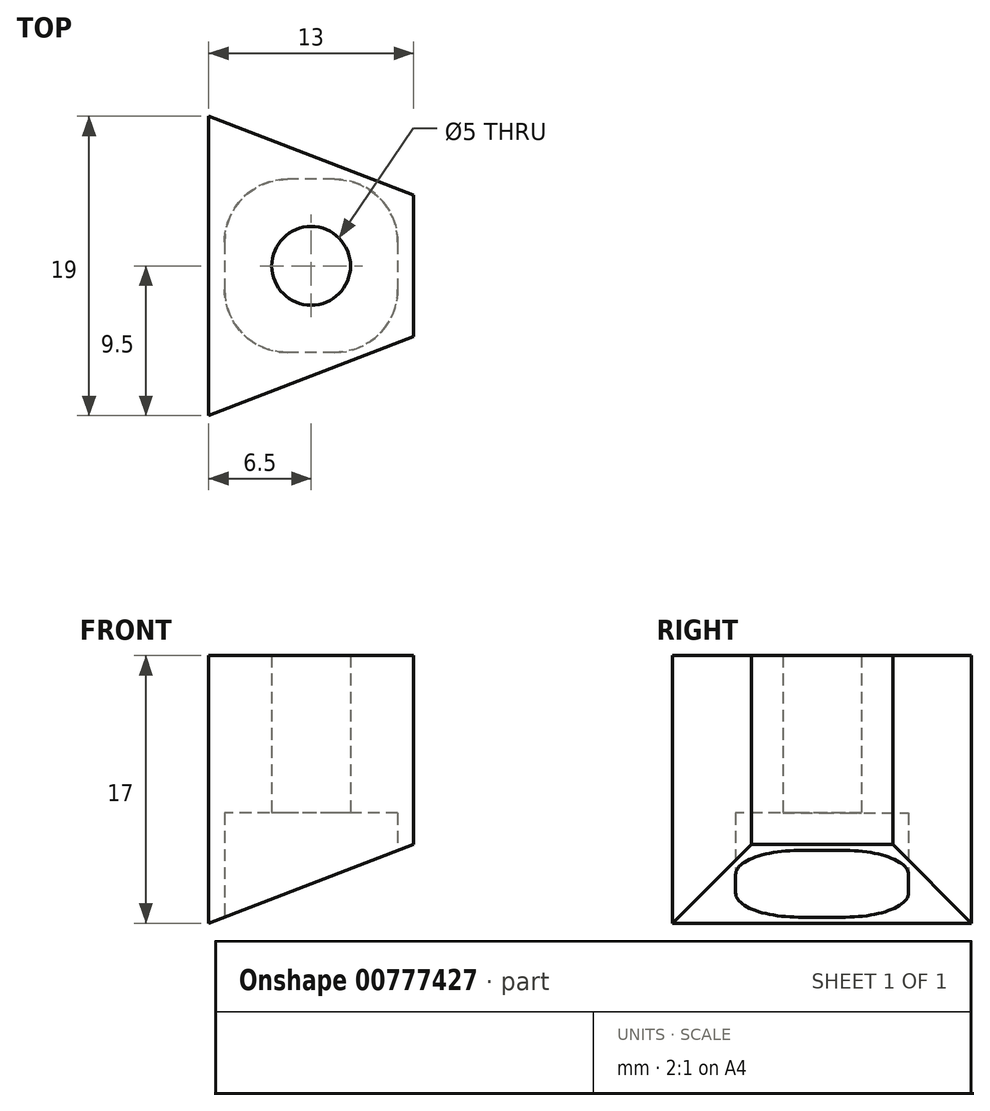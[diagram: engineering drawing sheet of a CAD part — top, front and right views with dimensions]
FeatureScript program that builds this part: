
annotation { "Feature Type Name" : "Feature", "Feature Type Description" : "" }
export const myFeature = defineFeature(function(context is Context, id is Id, definition is map)
    precondition{}
    {
        {
            var Q0;
            Q0=qCreatedBy(makeId("Front.planeOp"),FACE);
            var sketch = newSketch(context, id + "F0", { "sketchPlane" : qUnion([Q0])});
            skLineSegment(sketch, "E0", {"start": v(0, 0) * mm, "end": v(0, 17) * mm});
            skLineSegment(sketch, "E1", {"start": v(0, 17) * mm, "end": v(13, 17) * mm});
            skLineSegment(sketch, "E2", {"start": v(13, 17) * mm, "end": v(13, 5) * mm});
            skLineSegment(sketch, "E3", {"start": v(13, 5) * mm, "end": v(0, 0) * mm});
            skSolve(sketch);
        }
        {
            var Q0;
            Q0 = qSketchRegion(id + "F0", true);
            extrude(context, id + "F1", {"entities" : qUnion([Q0]), "endBound" : BoundingType.SYMMETRIC, "depth" : 19 * mm, "offsetDistance" : 25 * mm});
        }
        {
            var Q0;
            Q0=makeQuery(id+"F1.opExtrude","SWEPT_FACE",FACE,{"disambiguationData":[OSD([sQuery(id+"F0.wireOp",EDGE,"E1")])]});
            var sketch = newSketch(context, id + "F2", { "sketchPlane" : qUnion([Q0])});
            skLineSegment(sketch, "E4", {"start": v(0, 9.5) * mm, "end": v(13, 9.5) * mm});
            skLineSegment(sketch, "E5", {"start": v(13, 9.5) * mm, "end": v(13, 4.5) * mm});
            skLineSegment(sketch, "E6", {"start": v(13, 4.5) * mm, "end": v(0, 9.5) * mm});
            skLineSegment(sketch, "E7", {"start": v(0, 0) * mm, "end": v(16.47, 0) * mm, "construction": true});
            skLineSegment(sketch, "E8.MirrorCS", {"start": v(13, -4.5) * mm, "end": v(0, -9.5) * mm});
            skLineSegment(sketch, "E9.MirrorCS", {"start": v(0, -9.5) * mm, "end": v(13, -9.5) * mm});
            skLineSegment(sketch, "E10.MirrorCS", {"start": v(13, -9.5) * mm, "end": v(13, -4.5) * mm});
            skSolve(sketch);
        }
        {
            var Q0;
            Q0 = qSketchRegion(id + "F2", true);
            extrude(context, id + "F3", {"entities" : qUnion([Q0]), "operationType" : NewBodyOperationType.REMOVE, "oppositeDirection" : true, "depth" : 25 * mm, "offsetDistance" : 25 * mm});
        }
        {
            var Q0;
            Q0=qCreatedBy(makeId("Top.planeOp"),FACE);
            var sketch = newSketch(context, id + "F4", { "sketchPlane" : qUnion([Q0])});
            skLineSegment(sketch, "E11.bottom", {"start": v(8, 5.5) * mm, "end": v(5, 5.5) * mm});
            skLineSegment(sketch, "E11.top", {"start": v(8, -5.5) * mm, "end": v(5, -5.5) * mm});
            skLineSegment(sketch, "E11.left", {"start": v(12, 1.5) * mm, "end": v(12, -1.5) * mm});
            skLineSegment(sketch, "E11.right", {"start": v(1, 1.5) * mm, "end": v(1, -1.5) * mm});
            skPoint(sketch, "E11.middle", {"position": v(6.5, 0) * mm});
            skLineSegment(sketch, "E12", {"start": v(0, 0) * mm, "end": v(13, 0) * mm, "construction": true});
            skPoint(sketch, "E13.visualSharp", {"position": v(1, 5.5) * mm});
            skArc(sketch, "E13.filletArc", {"start": v(5, 5.5) * mm, "mid": v(2.17, 4.33) * mm, "end": v(1, 1.5) * mm});
            skPoint(sketch, "E14.visualSharp", {"position": v(12, 5.5) * mm});
            skArc(sketch, "E14.filletArc", {"start": v(12, 1.5) * mm, "mid": v(10.83, 4.33) * mm, "end": v(8, 5.5) * mm});
            skPoint(sketch, "E15.visualSharp", {"position": v(12, -5.5) * mm});
            skArc(sketch, "E15.filletArc", {"start": v(8, -5.5) * mm, "mid": v(10.83, -4.33) * mm, "end": v(12, -1.5) * mm});
            skPoint(sketch, "E16.visualSharp", {"position": v(1, -5.5) * mm});
            skArc(sketch, "E16.filletArc", {"start": v(1, -1.5) * mm, "mid": v(2.17, -4.33) * mm, "end": v(5, -5.5) * mm});
            skCircle(sketch, "E17", {"center": v(6.5, 0) * mm, "radius": 2.5 * mm});
            skSolve(sketch);
        }
        {
            var Q0;
            Q0 = qSketchRegion(id + "F4", true);
            extrude(context, id + "F5", {"entities" : qUnion([Q0]), "operationType" : NewBodyOperationType.REMOVE, "depth" : 7 * mm, "offsetDistance" : 25 * mm});
        }
        {
            var Q0;
            Q0=makeQuery(id+"F4.imprint","IMPRINT",FACE,{"disambiguationData":[TD([[makeQuery(id+"F4.imprint","IMPRINT",EDGE,{"derivedFrom":sQuery(id+"F4.wireOp",EDGE,"E17")}),1.0]])]});
            extrude(context, id + "F6", {"entities" : qUnion([Q0]), "operationType" : NewBodyOperationType.REMOVE, "depth" : 25 * mm, "offsetDistance" : 25 * mm});
        }
    });
